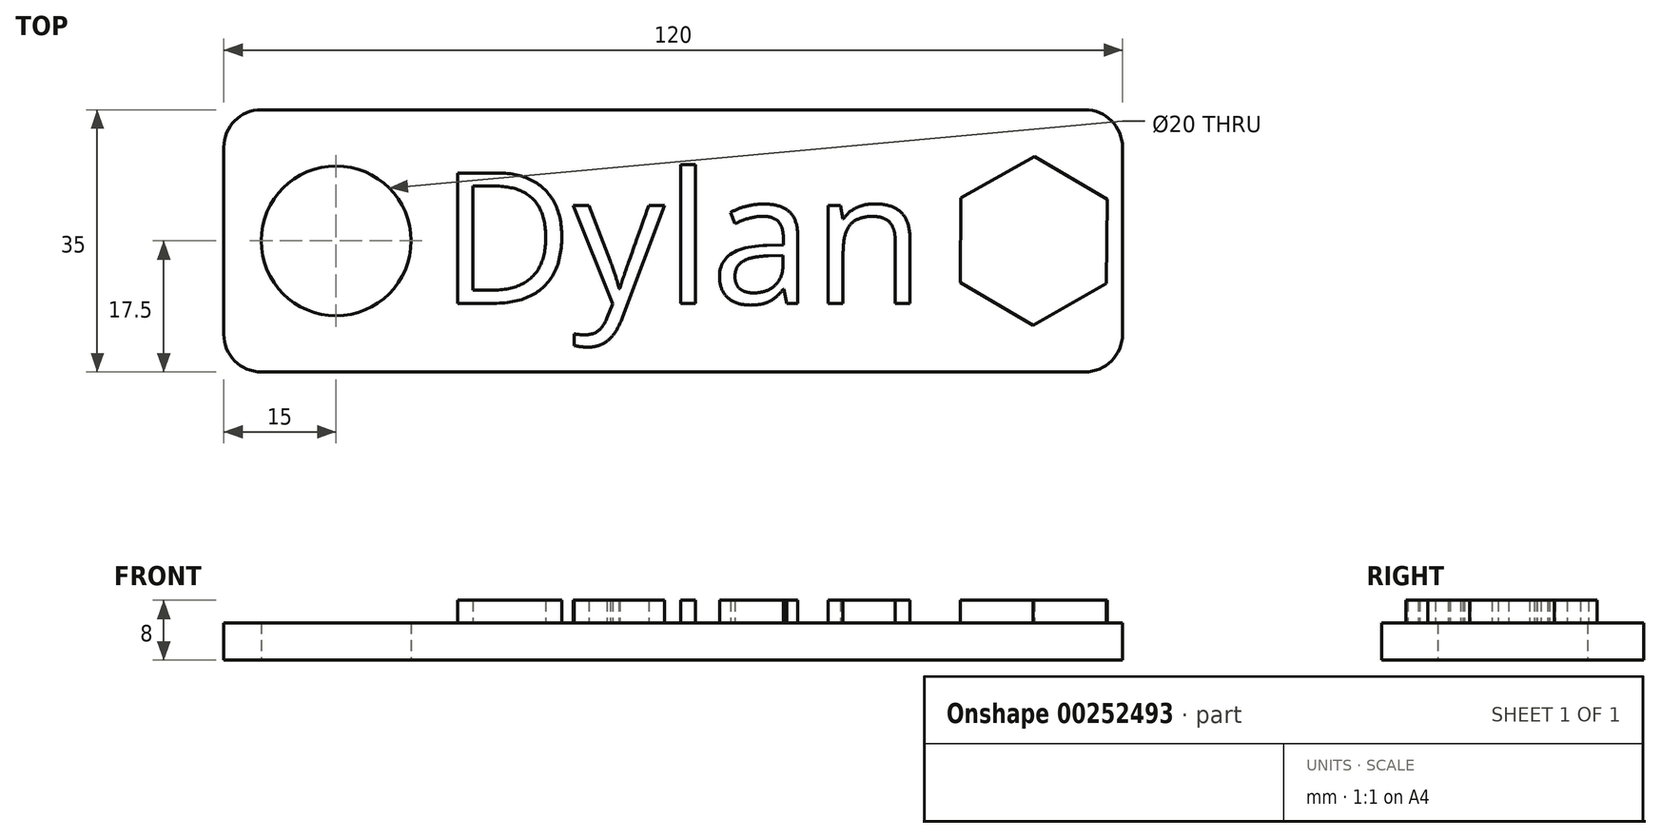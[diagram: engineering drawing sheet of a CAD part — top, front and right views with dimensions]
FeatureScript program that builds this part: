
annotation { "Feature Type Name" : "Feature", "Feature Type Description" : "" }
export const myFeature = defineFeature(function(context is Context, id is Id, definition is map)
    precondition{}
    {
        {
            var Q0;
            Q0=qCreatedBy(makeId("Top.planeOp"),FACE);
            var sketch = newSketch(context, id + "F0", { "sketchPlane" : qUnion([Q0])});
            skLineSegment(sketch, "E0.bottom", {"start": v(60, -17.5) * mm, "end": v(-60, -17.5) * mm});
            skLineSegment(sketch, "E0.top", {"start": v(60, 17.5) * mm, "end": v(-60, 17.5) * mm});
            skLineSegment(sketch, "E0.left", {"start": v(60, -17.5) * mm, "end": v(60, 17.5) * mm});
            skLineSegment(sketch, "E0.right", {"start": v(-60, -17.5) * mm, "end": v(-60, 17.5) * mm});
            skPoint(sketch, "E0.middle", {"position": v(0, 0) * mm});
            skCircle(sketch, "E1", {"center": v(-45, 0) * mm, "radius": 10 * mm});
            skSolve(sketch);
        }
        {
            var Q0;
            Q0=makeQuery(id+"F0.imprint","IMPRINT",FACE,{"disambiguationData":[TD([[makeQuery(id+"F0.imprint","IMPRINT",EDGE,{"derivedFrom":sQuery(id+"F0.wireOp",EDGE,"E0.bottom")}),-1.0]])]});
            extrude(context, id + "F1", {"entities" : qUnion([Q0]), "depth" : 5 * mm});
        }
        {
            var Q0;
            Q0=makeQuery(id+"F1.opExtrude","SWEPT_EDGE",EDGE,{"disambiguationData":[OSD([sQuery(id+"F0.wireOp",EDGE,"E0.top"),sQuery(id+"F0.wireOp",EDGE,"E0.right")])]});
            var Q1;
            Q1=makeQuery(id+"F1.opExtrude","SWEPT_EDGE",EDGE,{"disambiguationData":[OSD([sQuery(id+"F0.wireOp",EDGE,"E0.bottom"),sQuery(id+"F0.wireOp",EDGE,"E0.right")])]});
            var Q2;
            Q2=makeQuery(id+"F1.opExtrude","SWEPT_EDGE",EDGE,{"disambiguationData":[OSD([sQuery(id+"F0.wireOp",EDGE,"E0.bottom"),sQuery(id+"F0.wireOp",EDGE,"E0.left")])]});
            var Q3;
            Q3=makeQuery(id+"F1.opExtrude","SWEPT_EDGE",EDGE,{"disambiguationData":[OSD([sQuery(id+"F0.wireOp",EDGE,"E0.top"),sQuery(id+"F0.wireOp",EDGE,"E0.left")])]});
            fillet(context, id + "F2", {"entities" : qUnion([Q0, Q1, Q2, Q3]), "radius" : 5 * mm, "tangentPropagation" : true, "allowEdgeOverflow" : false});
        }
        {
            var Q0;
            Q0=makeQuery(id+"F1.opExtrude","CAP_FACE",FACE,{"disambiguationData":[OSD([sQuery(id+"F0.wireOp",EDGE,"E0.bottom"),sQuery(id+"F0.wireOp",EDGE,"E0.top"),sQuery(id+"F0.wireOp",EDGE,"E0.left"),sQuery(id+"F0.wireOp",EDGE,"E0.right"),sQuery(id+"F0.wireOp",EDGE,"E1")])],"isStart":false});
            var sketch = newSketch(context, id + "F3", { "sketchPlane" : qUnion([Q0])});
            skText(sketch, "E2", { "text": "Dylan", "fontName": "OpenSans-Regular.ttf"});
            const initialGuessF3  = {"E2": [-0.03115, -0.00834, 1, 0, 0.01755]};
            skSetInitialGuess(sketch, initialGuessF3);
            skSolve(sketch);
        }
        {
            var Q0;
            Q0 = qSketchRegion(id + "F3", true);
            extrude(context, id + "F4", {"entities" : qUnion([Q0]), "operationType" : NewBodyOperationType.ADD, "depth" : 3 * mm});
        }
        {
            var Q0;
            {var subQ0=sQuery(id+"F0.wireOp",EDGE,"E0.top");var subQ1=sQuery(id+"F0.wireOp",EDGE,"E0.left");var subQ2=sQuery(id+"F0.wireOp",EDGE,"E0.bottom");var subQ3=sQuery(id+"F0.wireOp",EDGE,"E1");var subQ4=sQuery(id+"F0.wireOp",EDGE,"E0.right");Q0=makeQuery(id+"F4.boolean.opBoolean","SPLIT",FACE,{"disambiguationData":[TD([makeQuery(id+"F1.opExtrude","SWEPT_FACE",FACE,{"disambiguationData":[OSD([subQ2])]})])],"derivedFrom":makeQuery(id+"F1.opExtrude","CAP_FACE",FACE,{"disambiguationData":[OSD([subQ2,subQ0,subQ1,subQ4,subQ3])],"isStart":false})});}
            var sketch = newSketch(context, id + "F5", { "sketchPlane" : qUnion([Q0])});
            skCircle(sketch, "E3.cCircle", {"center": v(48.16, 0) * mm, "radius": 9.77 * mm, "construction": true});
            skLineSegment(sketch, "E3.0", {"start": v(38.43, 5.72) * mm, "end": v(48.25, 11.28) * mm});
            skLineSegment(sketch, "E3.1", {"start": v(48.25, 11.28) * mm, "end": v(57.97, 5.56) * mm});
            skLineSegment(sketch, "E3.2", {"start": v(57.97, 5.56) * mm, "end": v(57.88, -5.72) * mm});
            skLineSegment(sketch, "E3.3", {"start": v(57.88, -5.72) * mm, "end": v(48.07, -11.28) * mm});
            skLineSegment(sketch, "E3.4", {"start": v(48.07, -11.28) * mm, "end": v(38.34, -5.56) * mm});
            skLineSegment(sketch, "E3.5", {"start": v(38.34, -5.56) * mm, "end": v(38.43, 5.72) * mm});
            skPoint(sketch, "E3.0.midPoint", {"position": v(43.34, 8.5) * mm});
            skSolve(sketch);
        }
        {
            var Q0;
            Q0=makeQuery(id+"F5.imprint","IMPRINT",FACE,{"disambiguationData":[TD([[makeQuery(id+"F5.imprint","IMPRINT",EDGE,{"derivedFrom":sQuery(id+"F5.wireOp",EDGE,"E3.0")}),-1.0]])]});
            extrude(context, id + "F6", {"entities" : qUnion([Q0]), "operationType" : NewBodyOperationType.ADD, "depth" : 3 * mm});
        }
    });
